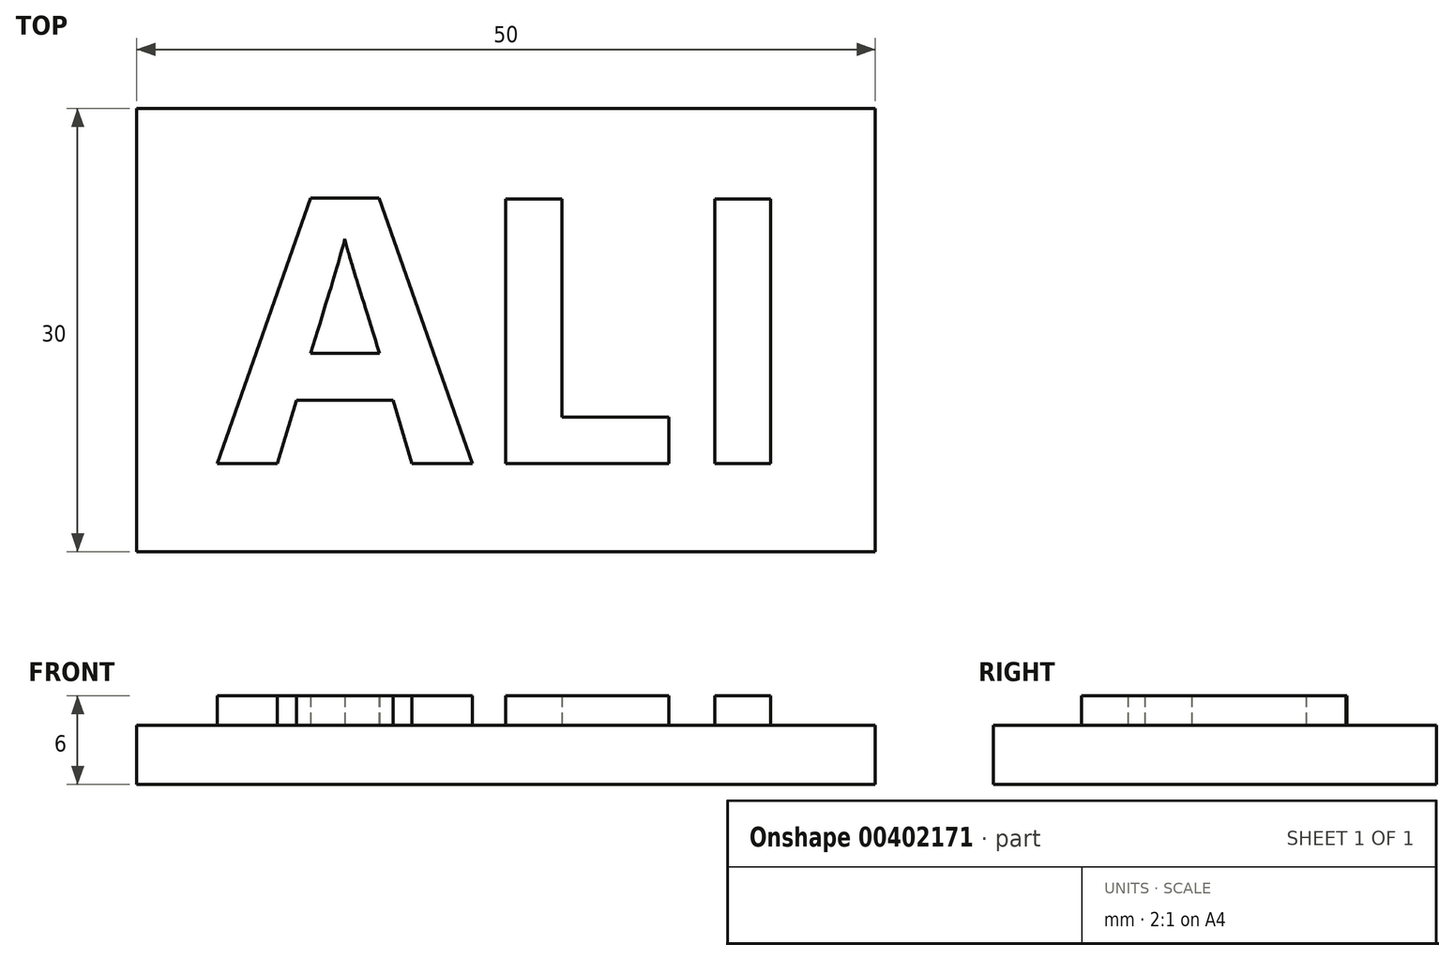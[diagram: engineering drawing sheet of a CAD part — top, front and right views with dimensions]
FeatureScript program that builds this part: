
annotation { "Feature Type Name" : "Feature", "Feature Type Description" : "" }
export const myFeature = defineFeature(function(context is Context, id is Id, definition is map)
    precondition{}
    {
        {
            var Q0;
            Q0=qCreatedBy(makeId("Top.planeOp"),FACE);
            var sketch = newSketch(context, id + "F0", { "sketchPlane" : qUnion([Q0])});
            skLineSegment(sketch, "E0.bottom", {"start": v(25, -15) * mm, "end": v(-25, -15) * mm});
            skLineSegment(sketch, "E0.top", {"start": v(25, 15) * mm, "end": v(-25, 15) * mm});
            skLineSegment(sketch, "E0.left", {"start": v(25, -15) * mm, "end": v(25, 15) * mm});
            skLineSegment(sketch, "E0.right", {"start": v(-25, -15) * mm, "end": v(-25, 15) * mm});
            skPoint(sketch, "E0.middle", {"position": v(0, 0) * mm});
            skSolve(sketch);
        }
        {
            var Q0;
            Q0 = qSketchRegion(id + "F0", true);
            extrude(context, id + "F1", {"entities" : qUnion([Q0]), "depth" : 4 * mm});
        }
        {
            var Q0;
            Q0=makeQuery(id+"F1.opExtrude","CAP_FACE",FACE,{"disambiguationData":[OSD([sQuery(id+"F0.wireOp",EDGE,"E0.bottom"),sQuery(id+"F0.wireOp",EDGE,"E0.top"),sQuery(id+"F0.wireOp",EDGE,"E0.left"),sQuery(id+"F0.wireOp",EDGE,"E0.right")])],"isStart":false});
            var sketch = newSketch(context, id + "F2", { "sketchPlane" : qUnion([Q0])});
            skText(sketch, "E1", { "text": "ALI", "fontName": "OpenSans-Bold.ttf"});
            const initialGuessF2  = {"E1": [-0.01956, -0.00902, 1, 0, 0.01804]};
            skSetInitialGuess(sketch, initialGuessF2);
            skSolve(sketch);
        }
        {
            var Q0;
            Q0 = qSketchRegion(id + "F2", true);
            extrude(context, id + "F3", {"entities" : qUnion([Q0]), "operationType" : NewBodyOperationType.ADD, "depth" : 2 * mm});
        }
    });
